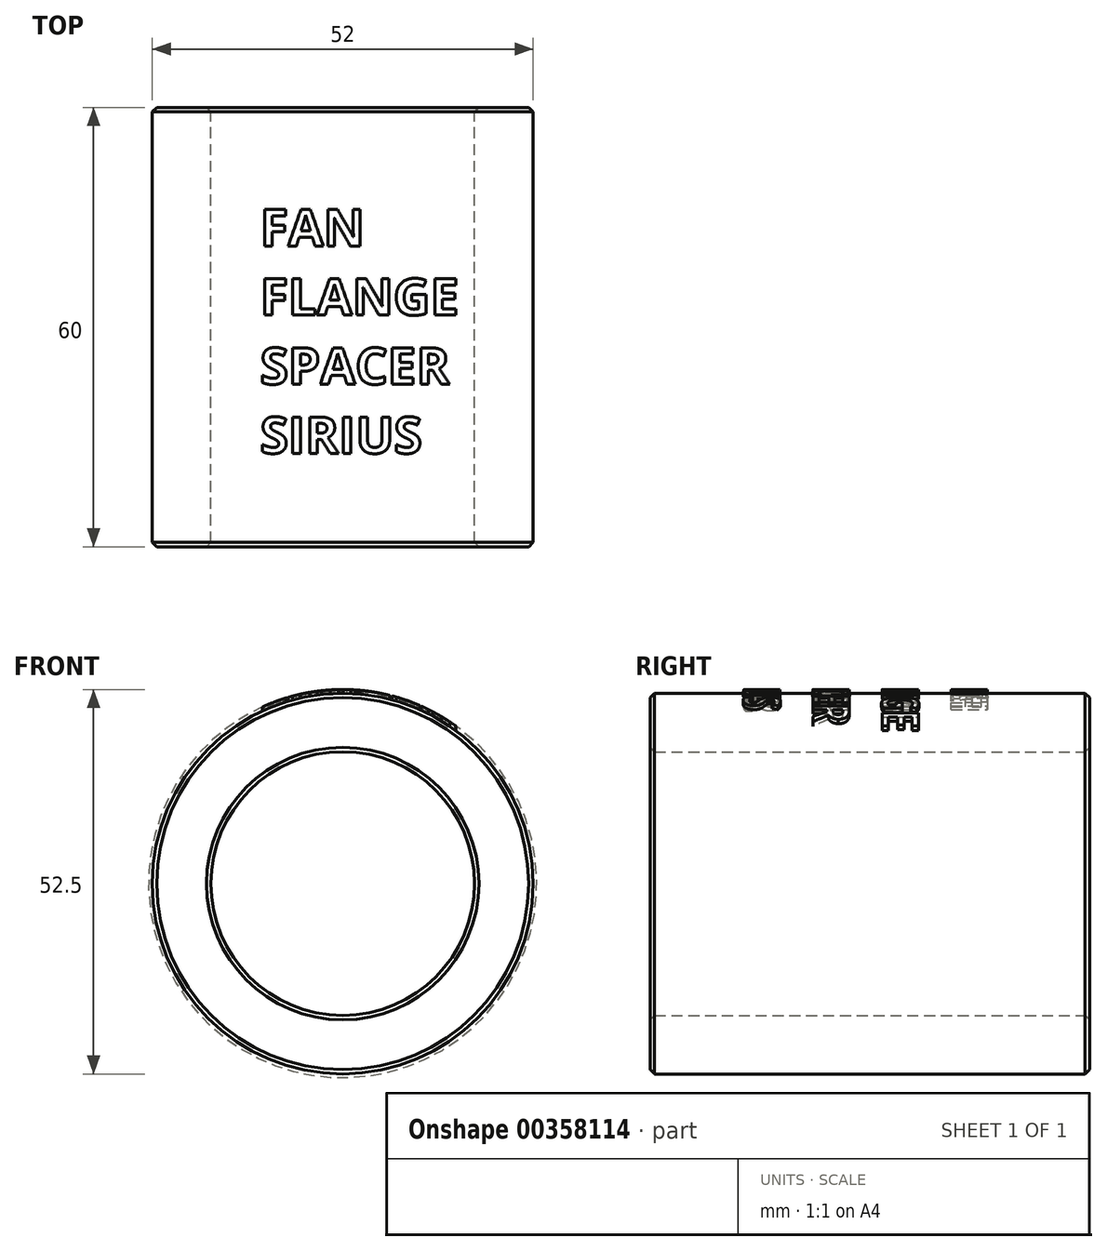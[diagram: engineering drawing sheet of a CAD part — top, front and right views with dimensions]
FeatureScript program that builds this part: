
annotation { "Feature Type Name" : "Feature", "Feature Type Description" : "" }
export const myFeature = defineFeature(function(context is Context, id is Id, definition is map)
    precondition{}
    {
        {
            var Q0;
            Q0=qCreatedBy(makeId("Front.planeOp"),FACE);
            var sketch = newSketch(context, id + "F0", { "sketchPlane" : qUnion([Q0])});
            skCircle(sketch, "E0", {"center": v(0, 0) * mm, "radius": 18 * mm});
            skCircle(sketch, "E1", {"center": v(0, 0) * mm, "radius": 26 * mm});
            skSolve(sketch);
        }
        {
            var Q0;
            Q0 = qSketchRegion(id + "F0", true);
            extrude(context, id + "F1", {"entities" : qUnion([Q0]), "depth" : 60 * mm});
        }
        {
            var Q0;
            Q0=makeQuery(id+"F1.opExtrude","CAP_EDGE",EDGE,{"disambiguationData":[OSD([sQuery(id+"F0.wireOp",EDGE,"E1")])],"isStart":true});
            var Q1;
            Q1=makeQuery(id+"F1.opExtrude","CAP_EDGE",EDGE,{"disambiguationData":[OSD([sQuery(id+"F0.wireOp",EDGE,"E0")])],"isStart":true});
            var Q2;
            Q2=makeQuery(id+"F1.opExtrude","CAP_EDGE",EDGE,{"disambiguationData":[OSD([sQuery(id+"F0.wireOp",EDGE,"E0")])],"isStart":false});
            var Q3;
            Q3=makeQuery(id+"F1.opExtrude","CAP_EDGE",EDGE,{"disambiguationData":[OSD([sQuery(id+"F0.wireOp",EDGE,"E1")])],"isStart":false});
            chamfer(context, id + "F2", {"entities" : qUnion([Q0, Q1, Q2, Q3]), "width" : 0.6 * mm, "tangentPropagation" : true});
        }
        {
            var Q0;
            Q0=qCreatedBy(makeId("Top.planeOp"),FACE);
            cPlane(context, id + "F3", {"entities" : qUnion([Q0]), "cplaneType" : CPlaneType.OFFSET, "offset" : 30 * mm, "width" : 150 * mm, "height" : 150 * mm});
        }
        {
            var Q0;
            Q0=qCreatedBy(id+"F3.planeOp",FACE);
            var sketch = newSketch(context, id + "F4", { "sketchPlane" : qUnion([Q0])});
            skText(sketch, "E2", { "text": "FAN\nFLANGE \nSPACER\nSIRIUS", "fontName": "OpenSans-Bold.ttf"});
            const initialGuessF4  = {"E2": [-0.01125, -0.0189, 1, 0, 0.005]};
            skSetInitialGuess(sketch, initialGuessF4);
            skSolve(sketch);
        }
        {
            var Q0;
            Q0 = qSketchRegion(id + "F4", true);
            extrude(context, id + "F5", {"entities" : qUnion([Q0]), "operationType" : NewBodyOperationType.ADD, "endBound" : BoundingType.UP_TO_NEXT, "oppositeDirection" : true, "depth" : 25 * mm});
        }
        {
            var Q0;
            Q0=makeQuery(id+"F1.opExtrude","CAP_FACE",FACE,{"disambiguationData":[OSD([sQuery(id+"F0.wireOp",EDGE,"E0"),sQuery(id+"F0.wireOp",EDGE,"E1")])],"isStart":true});
            var sketch = newSketch(context, id + "F6", { "sketchPlane" : qUnion([Q0])});
            skCircle(sketch, "E3", {"center": v(0, 0) * mm, "radius": 26.5 * mm});
            skCircle(sketch, "E4", {"center": v(0, 0) * mm, "radius": 35 * mm});
            skSolve(sketch);
        }
        {
            var Q0;
            Q0=makeQuery(id+"F6.imprint","IMPRINT",FACE,{"disambiguationData":[TD([[makeQuery(id+"F6.imprint","IMPRINT",EDGE,{"derivedFrom":sQuery(id+"F6.wireOp",EDGE,"E3")}),-1.0]])]});
            extrude(context, id + "F7", {"entities" : qUnion([Q0]), "operationType" : NewBodyOperationType.REMOVE, "endBound" : BoundingType.THROUGH_ALL, "oppositeDirection" : true, "depth" : 25 * mm});
        }
    });
